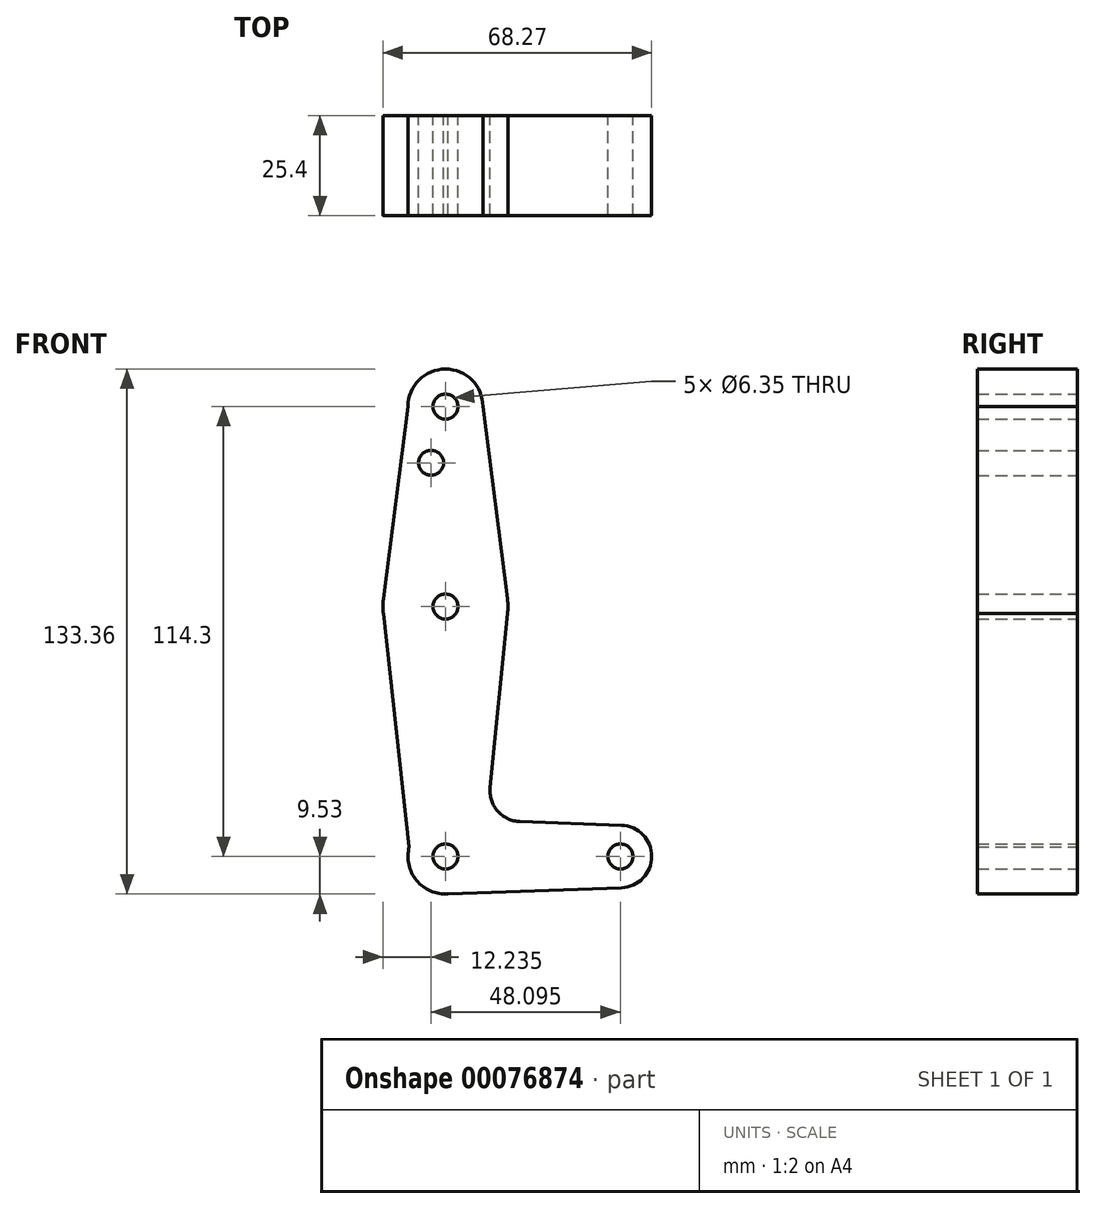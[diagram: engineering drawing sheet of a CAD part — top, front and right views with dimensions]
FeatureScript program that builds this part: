
annotation { "Feature Type Name" : "Feature", "Feature Type Description" : "" }
export const myFeature = defineFeature(function(context is Context, id is Id, definition is map)
    precondition{}
    {
        {
            var Q0;
            Q0=qCreatedBy(makeId("Front.planeOp"),FACE);
            var sketch = newSketch(context, id + "F0", { "sketchPlane" : qUnion([Q0])});
            skCircle(sketch, "E0", {"center": v(0, 0) * mm, "radius": 9.53 * mm});
            skLineSegment(sketch, "E1", {"start": v(0, 0) * mm, "end": v(0, 114.3) * mm, "construction": true});
            skLineSegment(sketch, "E2", {"start": v(0, 0) * mm, "end": v(44.45, 0) * mm, "construction": true});
            skCircle(sketch, "E3", {"center": v(44.45, 0) * mm, "radius": 7.94 * mm});
            skCircle(sketch, "E4", {"center": v(0, 114.3) * mm, "radius": 9.53 * mm});
            skCircle(sketch, "E5", {"center": v(0, 63.5) * mm, "radius": 15.88 * mm});
            skLineSegment(sketch, "E6", {"start": v(-9.53, 114.3) * mm, "end": v(-15.75, 65.5) * mm});
            skLineSegment(sketch, "E7", {"start": v(0, -9.53) * mm, "end": v(44.73, -7.93) * mm});
            skCircle(sketch, "E8", {"center": v(0, 114.3) * mm, "radius": 3.18 * mm});
            skCircle(sketch, "E9", {"center": v(0, 63.5) * mm, "radius": 3.18 * mm});
            skCircle(sketch, "E10", {"center": v(0, 0) * mm, "radius": 3.18 * mm});
            skCircle(sketch, "E11", {"center": v(44.45, 0) * mm, "radius": 3.18 * mm});
            skCircle(sketch, "E12", {"center": v(-3.64, 100.03) * mm, "radius": 3.18 * mm});
            skLineSegment(sketch, "E13", {"start": v(9.53, 114.3) * mm, "end": v(15.75, 65.5) * mm});
            skLineSegment(sketch, "E14", {"start": v(18.97, 8.85) * mm, "end": v(44.73, 7.93) * mm});
            skLineSegment(sketch, "E15", {"start": v(15.78, 61.75) * mm, "end": v(11.34, 17.59) * mm});
            skLineSegment(sketch, "E16", {"start": v(-15.78, 61.75) * mm, "end": v(-8.95, 0) * mm});
            skArc(sketch, "E17.filletArc", {"start": v(11.34, 17.59) * mm, "mid": v(13.26, 11.57) * mm, "end": v(18.97, 8.85) * mm});
            skSolve(sketch);
        }
        {
            var Q0;
            Q0 = qSketchRegion(id + "F0", true);
            extrude(context, id + "F1", {"entities" : qUnion([Q0]), "depth" : 25.4 * mm});
        }
    });
